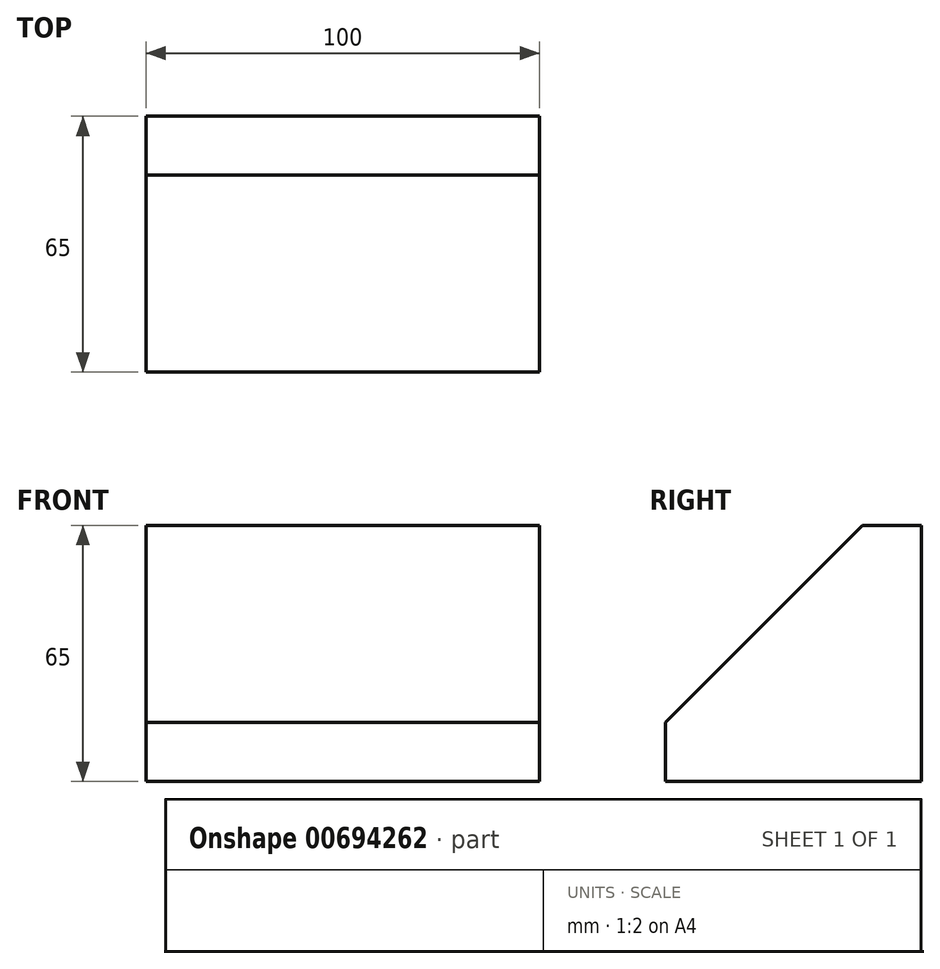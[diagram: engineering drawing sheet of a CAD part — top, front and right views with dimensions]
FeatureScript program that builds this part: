
annotation { "Feature Type Name" : "Feature", "Feature Type Description" : "" }
export const myFeature = defineFeature(function(context is Context, id is Id, definition is map)
    precondition{}
    {
        {
            var Q0;
            Q0=qCreatedBy(makeId("Top.planeOp"),FACE);
            var sketch = newSketch(context, id + "F0", { "sketchPlane" : qUnion([Q0])});
            skLineSegment(sketch, "E0.bottom", {"start": v(-50, 32.5) * mm, "end": v(50, 32.5) * mm});
            skLineSegment(sketch, "E0.top", {"start": v(-50, -32.5) * mm, "end": v(50, -32.5) * mm});
            skLineSegment(sketch, "E0.left", {"start": v(-50, 32.5) * mm, "end": v(-50, -32.5) * mm});
            skLineSegment(sketch, "E0.right", {"start": v(50, 32.5) * mm, "end": v(50, -32.5) * mm});
            skSolve(sketch);
        }
        {
            var Q0;
            Q0=makeQuery(id+"F0.imprint","IMPRINT",FACE,{"disambiguationData":[TD([[makeQuery(id+"F0.imprint","IMPRINT",EDGE,{"derivedFrom":sQuery(id+"F0.wireOp",EDGE,"E0.bottom")}),-1.0]])]});
            extrude(context, id + "F1", {"entities" : qUnion([Q0]), "depth" : 65 * mm, "offsetDistance" : 25 * mm});
        }
        {
            var Q0;
            Q0=makeQuery(id+"F1.opExtrude","SWEPT_FACE",FACE,{"disambiguationData":[OSD([sQuery(id+"F0.wireOp",EDGE,"E0.right")])]});
            var sketch = newSketch(context, id + "F2", { "sketchPlane" : qUnion([Q0])});
            skLineSegment(sketch, "E1", {"start": v(-32.5, 0) * mm, "end": v(0, 0) * mm});
            skLineSegment(sketch, "E2", {"start": v(-32.5, 15) * mm, "end": v(-32.5, 0) * mm});
            skLineSegment(sketch, "E3", {"start": v(32.5, 65) * mm, "end": v(17.5, 65) * mm});
            skLineSegment(sketch, "E4", {"start": v(-32.5, 15) * mm, "end": v(17.5, 65) * mm});
            skSolve(sketch);
        }
        {
            var Q0;
            Q0 = qSketchRegion(id + "F2", true);
            var Q1;
            {var subQ0=sQuery(id+"F2.wireOp",EDGE,"E4");Q1=makeQuery(id+"F2.imprint","IMPRINT",FACE,{"disambiguationData":[TD([[makeQuery(id+"F2.imprint","IMPRINT",EDGE,{"derivedFrom":subQ0}),1.0]])]});}
            extrude(context, id + "F3", {"entities" : qUnion([Q0, Q1]), "operationType" : NewBodyOperationType.REMOVE, "endBound" : BoundingType.THROUGH_ALL, "oppositeDirection" : true, "depth" : 25 * mm, "offsetDistance" : 25 * mm});
        }
    });
